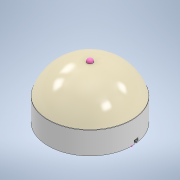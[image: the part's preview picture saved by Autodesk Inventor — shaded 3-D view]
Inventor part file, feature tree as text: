
AUTODESK INVENTOR PART (.ipt)
format: ipt  version: 2020 (Build 240168000, 168)  size: 222,720 bytes
history: native  units: mm
features: plane x6, sketch x5, revolve x2, extrude x2, shell x1
ambient origin geometry x8: Origin, YZ Plane, XZ Plane, XY Plane, X Axis, Y Axis, Z Axis, Center Point
bodies: Solid1 (feature_tree)
feature tree (16):
  revolve  "Revolution1"  [1 undecoded]
  shell  "Shell1"  Thickness=2.0mm
  plane  "Work Plane1"
  extrude  "Extrusion1"  Depth=2.0mm
  revolve  "Revolution2"  [1 undecoded]
  plane  "Work Plane2"
  plane  "Work Plane5"
  sketch  "Sketch5"  dims[d7=2.0mm d8=2.2mm]
  plane  "Work Plane4"
  plane  "Work Plane6"
  plane  "Work Plane7"
  extrude  "Extrusion4"  Depth=2.2mm
  sketch  "Sketch1"  dims[d0=40.0mm d1=50.0mm d2=2.0mm]
  sketch  "Sketch2"  dims[d3=90.0deg d4=2.0mm]
  sketch  "Sketch4"  dims[d5=3.5mm d6=1.3mm]
  sketch  "Sketch7"  dims[d9=10.0mm d10=0.0mm d17=180.0deg d35=3.5mm d36=1.3mm d37=10.0mm d38=0.0mm d11=0.5mm d12=0.872665mm]
note: 2 required parameter values undecoded (feature->parameter linkage not recoverable at this tier; creation-order binding heuristic only, values carry confidence <= 0.55)
